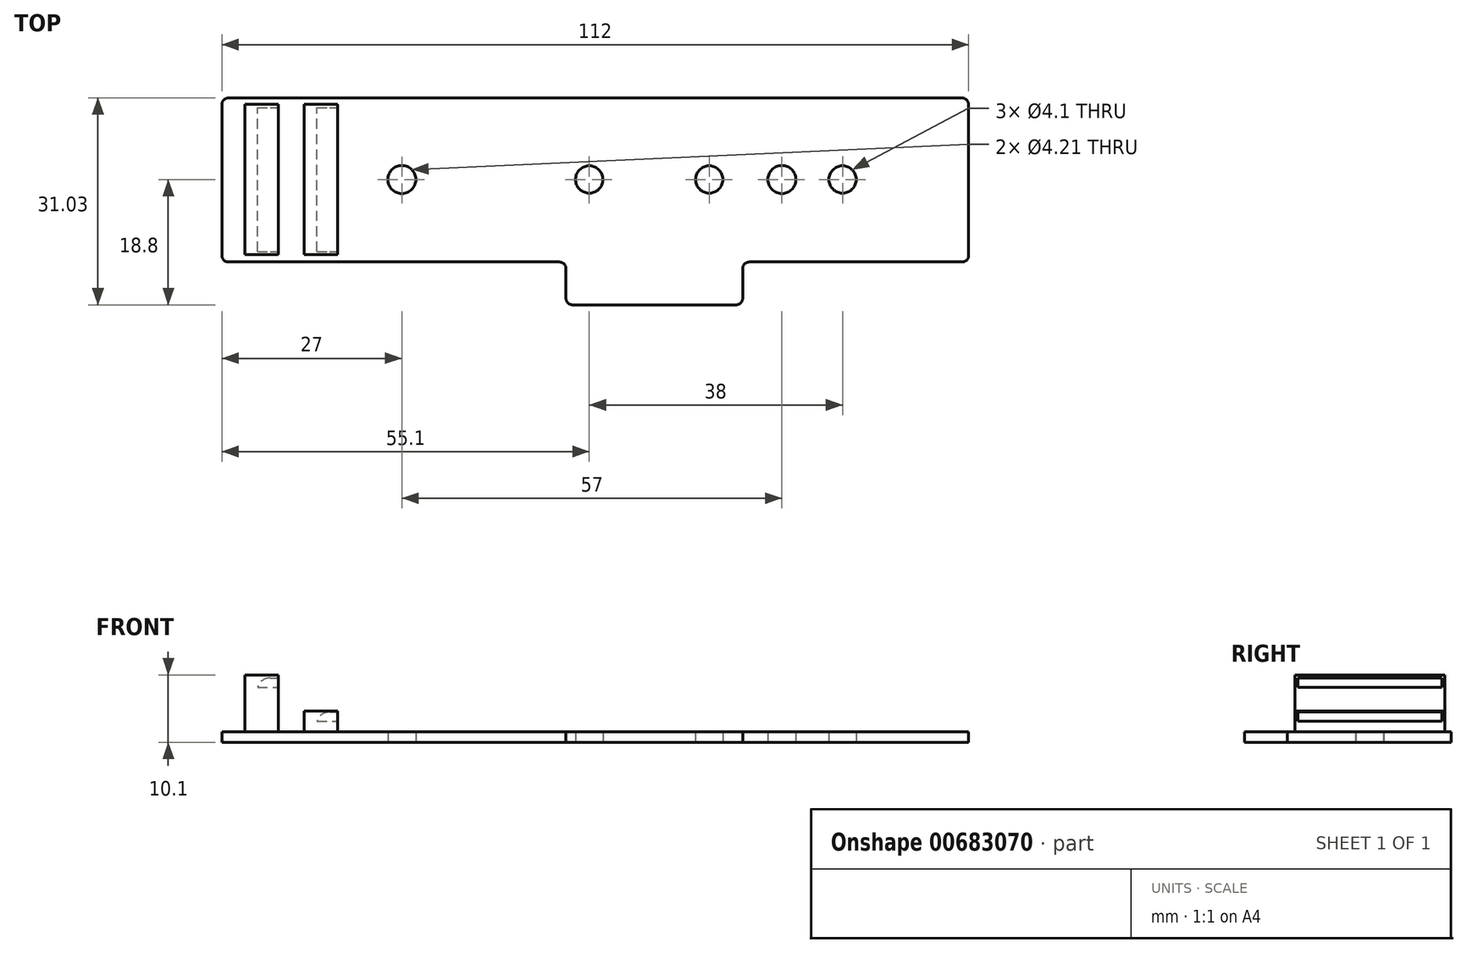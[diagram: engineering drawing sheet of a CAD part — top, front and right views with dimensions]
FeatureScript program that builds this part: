
annotation { "Feature Type Name" : "Feature", "Feature Type Description" : "" }
export const myFeature = defineFeature(function(context is Context, id is Id, definition is map)
    precondition{}
    {
        {
            assignVariable(context, id + "F0", {"name" : "M2conndepth", "anyValue" : 2.5});
        }
        {
            assignVariable(context, id + "F1", {"name" : "M2ssockheight", "anyValue" : 3.1});
        }
        {
            assignVariable(context, id + "F2", {"name" : "M2tsocketheight", "anyValue" : 8.5});
        }
        {
            assignVariable(context, id + "F3", {"name" : "PCBthick", "anyValue" : 1.6});
        }
        {
            var Q0;
            Q0=qCreatedBy(makeId("Top.planeOp"),FACE);
            var sketch = newSketch(context, id + "F4", { "sketchPlane" : qUnion([Q0])});
            skCircle(sketch, "E0", {"center": v(0, 0) * mm, "radius": 2.1 * mm});
            skLineSegment(sketch, "E1", {"start": v(0, 0) * mm, "end": v(-27, 0) * mm, "construction": true});
            skLineSegment(sketch, "E2", {"start": v(0, 0) * mm, "end": v(85, 0) * mm, "construction": true});
            skLineSegment(sketch, "E3.bottom", {"start": v(-27, 12.23) * mm, "end": v(85, 12.23) * mm});
            skLineSegment(sketch, "E3.top", {"start": v(-27, -12.37) * mm, "end": v(85, -12.37) * mm});
            skLineSegment(sketch, "E3.left", {"start": v(-27, 12.23) * mm, "end": v(-27, -12.37) * mm});
            skLineSegment(sketch, "E3.right", {"start": v(85, 12.23) * mm, "end": v(85, -12.37) * mm});
            skLineSegment(sketch, "E4", {"start": v(0, 0) * mm, "end": v(0, -12.37) * mm, "construction": true});
            skLineSegment(sketch, "E5", {"start": v(0, 0) * mm, "end": v(0, 12.23) * mm, "construction": true});
            skLineSegment(sketch, "E6", {"start": v(-17.03, -12.37) * mm, "end": v(0, -12.37) * mm, "construction": true});
            skLineSegment(sketch, "E7.bottom", {"start": v(-17.03, -12.37) * mm, "end": v(22.42, -12.37) * mm});
            skLineSegment(sketch, "E7.top", {"start": v(-17.03, -18.8) * mm, "end": v(22.42, -18.8) * mm});
            skLineSegment(sketch, "E7.left", {"start": v(-17.03, -12.37) * mm, "end": v(-17.03, -18.8) * mm});
            skLineSegment(sketch, "E7.right", {"start": v(22.42, -12.37) * mm, "end": v(22.42, -18.8) * mm});
            skLineSegment(sketch, "E8", {"start": v(2.7, -18.8) * mm, "end": v(2.7, 0) * mm, "construction": true});
            skLineSegment(sketch, "E9", {"start": v(22.42, -18.8) * mm, "end": v(0, -18.8) * mm, "construction": true});
            skLineSegment(sketch, "E10", {"start": v(0, -22.98) * mm, "end": v(24.62, -22.98) * mm, "construction": true});
            skLineSegment(sketch, "E11.bottom", {"start": v(24.62, -18.8) * mm, "end": v(51.12, -18.8) * mm});
            skLineSegment(sketch, "E11.top", {"start": v(24.62, -12.37) * mm, "end": v(51.12, -12.37) * mm});
            skLineSegment(sketch, "E11.left", {"start": v(24.62, -18.8) * mm, "end": v(24.62, -12.37) * mm});
            skLineSegment(sketch, "E11.right", {"start": v(51.12, -18.8) * mm, "end": v(51.12, -12.37) * mm});
            skLineSegment(sketch, "E12", {"start": v(0, -27.13) * mm, "end": v(51.12, -27.13) * mm, "construction": true});
            skLineSegment(sketch, "E13", {"start": v(0, 29.48) * mm, "end": v(57, 29.48) * mm, "construction": true});
            skCircle(sketch, "E14", {"center": v(57, 0) * mm, "radius": 2.1 * mm});
            skLineSegment(sketch, "E15", {"start": v(0, 0) * mm, "end": v(28.1, 0) * mm, "construction": true});
            skCircle(sketch, "E16", {"center": v(28.1, 0) * mm, "radius": 2.05 * mm});
            skLineSegment(sketch, "E17", {"start": v(0, 3.77) * mm, "end": v(46.1, 3.77) * mm, "construction": true});
            skCircle(sketch, "E18", {"center": v(46.1, 0) * mm, "radius": 2.05 * mm});
            skLineSegment(sketch, "E19", {"start": v(0, 8.26) * mm, "end": v(66.1, 8.26) * mm, "construction": true});
            skCircle(sketch, "E20", {"center": v(66.1, 0) * mm, "radius": 2.05 * mm});
            skLineSegment(sketch, "E21", {"start": v(0, -12.37) * mm, "end": v(-17.03, -12.37) * mm, "construction": true});
            skSolve(sketch);
        }
        {
            var Q0;
            Q0=makeQuery(id+"F4.imprint","IMPRINT",FACE,{"disambiguationData":[TD([[makeQuery(id+"F4.imprint","IMPRINT",EDGE,{"derivedFrom":sQuery(id+"F4.wireOp",EDGE,"E7.bottom")}),-1.0]])]});
            var Q1;
            Q1=makeQuery(id+"F4.imprint","IMPRINT",FACE,{"disambiguationData":[TD([[makeQuery(id+"F4.imprint","IMPRINT",EDGE,{"derivedFrom":sQuery(id+"F4.wireOp",EDGE,"E11.bottom")}),1.0]])]});
            var Q2;
            Q2=makeQuery(id+"F4.imprint","IMPRINT",FACE,{"disambiguationData":[TD([[makeQuery(id+"F4.imprint","IMPRINT",EDGE,{"derivedFrom":sQuery(id+"F4.wireOp",EDGE,"E1Ta9aYJ-BLLR-yCvW-Tl3E-SsffV6xoofWQ.bottom")}),1.0]])]});
            var Q3;
            Q3=makeQuery(id+"F4.imprint","IMPRINT",FACE,{"disambiguationData":[TD([[makeQuery(id+"F4.imprint","IMPRINT",EDGE,{"derivedFrom":sQuery(id+"F4.wireOp",EDGE,"a8g1MiHS-Xpk4-FMXC-Xz5o-XKk2ycmWGk7U.bottom")}),1.0]])]});
            var Q4;
            Q4=makeQuery(id+"F4.imprint","IMPRINT",FACE,{"disambiguationData":[TD([[makeQuery(id+"F4.imprint","IMPRINT",EDGE,{"derivedFrom":sQuery(id+"F4.wireOp",EDGE,"YHdcBCCz-BpKQ-KRm3-anxo-6fSsjPzmbMLq.bottom")}),-1.0]])]});
            var Q5;
            Q5=makeQuery(id+"F4.imprint","IMPRINT",FACE,{"disambiguationData":[TD([[makeQuery(id+"F4.imprint","IMPRINT",EDGE,{"derivedFrom":sQuery(id+"F4.wireOp",EDGE,"E0")}),-1.0]])]});
            extrude(context, id + "F5", {"entities" : qUnion([Q0, Q1, Q2, Q3, Q4, Q5]), "depth" : (getVariable(context, 'PCBthick')) * mm});
        }
        {
            var Q0;
            Q0=makeQuery(id+"F5.opExtrude","CAP_FACE",FACE,{"disambiguationData":[OSD([sQuery(id+"F4.wireOp",EDGE,"E0"),sQuery(id+"F4.wireOp",EDGE,"E3.bottom"),sQuery(id+"F4.wireOp",EDGE,"E3.top"),sQuery(id+"F4.wireOp",EDGE,"E3.left"),sQuery(id+"F4.wireOp",EDGE,"E3.right"),sQuery(id+"F4.wireOp",EDGE,"E7.top"),sQuery(id+"F4.wireOp",EDGE,"E7.left"),sQuery(id+"F4.wireOp",EDGE,"E7.right"),sQuery(id+"F4.wireOp",EDGE,"E11.bottom"),sQuery(id+"F4.wireOp",EDGE,"E11.left"),sQuery(id+"F4.wireOp",EDGE,"E11.right"),sQuery(id+"F4.wireOp",EDGE,"E1Ta9aYJ-BLLR-yCvW-Tl3E-SsffV6xoofWQ.bottom"),sQuery(id+"F4.wireOp",EDGE,"E1Ta9aYJ-BLLR-yCvW-Tl3E-SsffV6xoofWQ.left"),sQuery(id+"F4.wireOp",EDGE,"E1Ta9aYJ-BLLR-yCvW-Tl3E-SsffV6xoofWQ.right"),sQuery(id+"F4.wireOp",EDGE,"a8g1MiHS-Xpk4-FMXC-Xz5o-XKk2ycmWGk7U.bottom"),sQuery(id+"F4.wireOp",EDGE,"a8g1MiHS-Xpk4-FMXC-Xz5o-XKk2ycmWGk7U.left"),sQuery(id+"F4.wireOp",EDGE,"a8g1MiHS-Xpk4-FMXC-Xz5o-XKk2ycmWGk7U.right"),sQuery(id+"F4.wireOp",EDGE,"YHdcBCCz-BpKQ-KRm3-anxo-6fSsjPzmbMLq.top"),sQuery(id+"F4.wireOp",EDGE,"YHdcBCCz-BpKQ-KRm3-anxo-6fSsjPzmbMLq.left"),sQuery(id+"F4.wireOp",EDGE,"YHdcBCCz-BpKQ-KRm3-anxo-6fSsjPzmbMLq.right"),sQuery(id+"F4.wireOp",EDGE,"E14"),sQuery(id+"F4.wireOp",EDGE,"fpiimDXm-HCbj-4bNC-FueZ-Qats7nAzrHHA"),sQuery(id+"F4.wireOp",EDGE,"E16"),sQuery(id+"F4.wireOp",EDGE,"E18"),sQuery(id+"F4.wireOp",EDGE,"E20"),sQuery(id+"F4.wireOp",EDGE,"mZ1ixk2W-VYTq-aw9L-fxjL-cpEzxSfOFke0.top"),sQuery(id+"F4.wireOp",EDGE,"mZ1ixk2W-VYTq-aw9L-fxjL-cpEzxSfOFke0.left"),sQuery(id+"F4.wireOp",EDGE,"mZ1ixk2W-VYTq-aw9L-fxjL-cpEzxSfOFke0.right")])],"isStart":false});
            var sketch = newSketch(context, id + "F6", { "sketchPlane" : qUnion([Q0])});
            skLineSegment(sketch, "E22.bottom", {"start": v(-14.65, 11.25) * mm, "end": v(-9.65, 11.25) * mm});
            skLineSegment(sketch, "E22.top", {"start": v(-14.65, -11.25) * mm, "end": v(-9.65, -11.25) * mm});
            skLineSegment(sketch, "E22.left", {"start": v(-14.65, 11.25) * mm, "end": v(-14.65, -11.25) * mm});
            skLineSegment(sketch, "E22.right", {"start": v(-9.65, 11.25) * mm, "end": v(-9.65, -11.25) * mm});
            skLineSegment(sketch, "E23.bottom", {"start": v(-23.55, -11.25) * mm, "end": v(-18.55, -11.25) * mm});
            skLineSegment(sketch, "E23.top", {"start": v(-23.55, 11.25) * mm, "end": v(-18.55, 11.25) * mm});
            skLineSegment(sketch, "E23.left", {"start": v(-23.55, -11.25) * mm, "end": v(-23.55, 11.25) * mm});
            skLineSegment(sketch, "E23.right", {"start": v(-18.55, -11.25) * mm, "end": v(-18.55, 11.25) * mm});
            skPoint(sketch, "E23.middle", {"position": v(-21.05, 0) * mm});
            skCircle(sketch, "E24.0", {"center": v(0, 0) * mm, "radius": 2.1 * mm, "construction": true});
            skLineSegment(sketch, "E25", {"start": v(0, 0) * mm, "end": v(-21.05, 0) * mm, "construction": true});
            skLineSegment(sketch, "E26", {"start": v(0, 0) * mm, "end": v(-12.15, 0) * mm});
            skLineSegment(sketch, "E27", {"start": v(-14.65, 11.25) * mm, "end": v(-9.65, -11.25) * mm, "construction": true});
            skPoint(sketch, "E28", {"position": v(-12.15, 0) * mm});
            skSolve(sketch);
        }
        {
            var Q0;
            Q0=makeQuery(id+"F6.imprint","IMPRINT",FACE,{"disambiguationData":[TD([[makeQuery(id+"F6.imprint","IMPRINT",EDGE,{"derivedFrom":sQuery(id+"F6.wireOp",EDGE,"E22.bottom")}),-1.0]])]});
            extrude(context, id + "F7", {"entities" : qUnion([Q0]), "operationType" : NewBodyOperationType.ADD, "depth" : (getVariable(context, 'M2ssockheight')) * mm, "offsetDistance" : 25 * mm});
        }
        {
            var Q0;
            Q0=makeQuery(id+"F6.imprint","IMPRINT",FACE,{"disambiguationData":[TD([[makeQuery(id+"F6.imprint","IMPRINT",EDGE,{"derivedFrom":sQuery(id+"F6.wireOp",EDGE,"E23.bottom")}),1.0]])]});
            extrude(context, id + "F8", {"entities" : qUnion([Q0]), "operationType" : NewBodyOperationType.ADD, "depth" : (getVariable(context, 'M2tsocketheight')) * mm, "offsetDistance" : 25 * mm});
        }
        {
            var Q0;
            Q0=makeQuery(id+"F5.opExtrude","SWEPT_EDGE",EDGE,{"disambiguationData":[OSD([sQuery(id+"F4.wireOp",EDGE,"E3.top"),sQuery(id+"F4.wireOp",EDGE,"E3.left")])]});
            var Q1;
            Q1=makeQuery(id+"F5.opExtrude","SWEPT_EDGE",EDGE,{"disambiguationData":[OSD([sQuery(id+"F4.wireOp",EDGE,"E3.top"),sQuery(id+"F4.wireOp",EDGE,"E7.bottom"),sQuery(id+"F4.wireOp",EDGE,"E7.left")])]});
            var Q2;
            Q2=makeQuery(id+"F5.opExtrude","SWEPT_EDGE",EDGE,{"disambiguationData":[OSD([sQuery(id+"F4.wireOp",EDGE,"E7.top"),sQuery(id+"F4.wireOp",EDGE,"E7.left")])]});
            var Q3;
            Q3=makeQuery(id+"F5.opExtrude","SWEPT_EDGE",EDGE,{"disambiguationData":[OSD([sQuery(id+"F4.wireOp",EDGE,"E3.top"),sQuery(id+"F4.wireOp",EDGE,"E11.top"),sQuery(id+"F4.wireOp",EDGE,"E11.left")])]});
            var Q4;
            Q4=makeQuery(id+"F5.opExtrude","SWEPT_EDGE",EDGE,{"disambiguationData":[OSD([sQuery(id+"F4.wireOp",EDGE,"E11.bottom"),sQuery(id+"F4.wireOp",EDGE,"E11.left")])]});
            var Q5;
            Q5=makeQuery(id+"F5.opExtrude","SWEPT_EDGE",EDGE,{"disambiguationData":[OSD([sQuery(id+"F4.wireOp",EDGE,"E7.top"),sQuery(id+"F4.wireOp",EDGE,"E7.right")])]});
            var Q6;
            Q6=makeQuery(id+"F5.opExtrude","SWEPT_EDGE",EDGE,{"disambiguationData":[OSD([sQuery(id+"F4.wireOp",EDGE,"E11.bottom"),sQuery(id+"F4.wireOp",EDGE,"E11.right")])]});
            var Q7;
            Q7=makeQuery(id+"F5.opExtrude","SWEPT_EDGE",EDGE,{"disambiguationData":[OSD([sQuery(id+"F4.wireOp",EDGE,"E3.top"),sQuery(id+"F4.wireOp",EDGE,"E1Ta9aYJ-BLLR-yCvW-Tl3E-SsffV6xoofWQ.top"),sQuery(id+"F4.wireOp",EDGE,"E1Ta9aYJ-BLLR-yCvW-Tl3E-SsffV6xoofWQ.left")])]});
            var Q8;
            Q8=makeQuery(id+"F5.opExtrude","SWEPT_EDGE",EDGE,{"disambiguationData":[OSD([sQuery(id+"F4.wireOp",EDGE,"E1Ta9aYJ-BLLR-yCvW-Tl3E-SsffV6xoofWQ.bottom"),sQuery(id+"F4.wireOp",EDGE,"E1Ta9aYJ-BLLR-yCvW-Tl3E-SsffV6xoofWQ.left")])]});
            var Q9;
            Q9=makeQuery(id+"F5.opExtrude","SWEPT_EDGE",EDGE,{"disambiguationData":[OSD([sQuery(id+"F4.wireOp",EDGE,"E1Ta9aYJ-BLLR-yCvW-Tl3E-SsffV6xoofWQ.bottom"),sQuery(id+"F4.wireOp",EDGE,"E1Ta9aYJ-BLLR-yCvW-Tl3E-SsffV6xoofWQ.right")])]});
            var Q10;
            Q10=makeQuery(id+"F5.opExtrude","SWEPT_EDGE",EDGE,{"disambiguationData":[OSD([sQuery(id+"F4.wireOp",EDGE,"a8g1MiHS-Xpk4-FMXC-Xz5o-XKk2ycmWGk7U.bottom"),sQuery(id+"F4.wireOp",EDGE,"a8g1MiHS-Xpk4-FMXC-Xz5o-XKk2ycmWGk7U.left")])]});
            var Q11;
            Q11=makeQuery(id+"F5.opExtrude","SWEPT_EDGE",EDGE,{"disambiguationData":[OSD([sQuery(id+"F4.wireOp",EDGE,"a8g1MiHS-Xpk4-FMXC-Xz5o-XKk2ycmWGk7U.bottom"),sQuery(id+"F4.wireOp",EDGE,"a8g1MiHS-Xpk4-FMXC-Xz5o-XKk2ycmWGk7U.right")])]});
            var Q12;
            Q12=makeQuery(id+"F5.opExtrude","SWEPT_EDGE",EDGE,{"disambiguationData":[OSD([sQuery(id+"F4.wireOp",EDGE,"E3.top"),sQuery(id+"F4.wireOp",EDGE,"YHdcBCCz-BpKQ-KRm3-anxo-6fSsjPzmbMLq.bottom"),sQuery(id+"F4.wireOp",EDGE,"YHdcBCCz-BpKQ-KRm3-anxo-6fSsjPzmbMLq.left")])]});
            var Q13;
            Q13=makeQuery(id+"F5.opExtrude","SWEPT_EDGE",EDGE,{"disambiguationData":[OSD([sQuery(id+"F4.wireOp",EDGE,"YHdcBCCz-BpKQ-KRm3-anxo-6fSsjPzmbMLq.top"),sQuery(id+"F4.wireOp",EDGE,"YHdcBCCz-BpKQ-KRm3-anxo-6fSsjPzmbMLq.left")])]});
            var Q14;
            Q14=makeQuery(id+"F5.opExtrude","SWEPT_EDGE",EDGE,{"disambiguationData":[OSD([sQuery(id+"F4.wireOp",EDGE,"E3.top"),sQuery(id+"F4.wireOp",EDGE,"E7.bottom"),sQuery(id+"F4.wireOp",EDGE,"E7.right")])]});
            var Q15;
            Q15=makeQuery(id+"F5.opExtrude","SWEPT_EDGE",EDGE,{"disambiguationData":[OSD([sQuery(id+"F4.wireOp",EDGE,"E3.top"),sQuery(id+"F4.wireOp",EDGE,"E11.top"),sQuery(id+"F4.wireOp",EDGE,"E11.right")])]});
            var Q16;
            Q16=makeQuery(id+"F5.opExtrude","SWEPT_EDGE",EDGE,{"disambiguationData":[OSD([sQuery(id+"F4.wireOp",EDGE,"mZ1ixk2W-VYTq-aw9L-fxjL-cpEzxSfOFke0.top"),sQuery(id+"F4.wireOp",EDGE,"mZ1ixk2W-VYTq-aw9L-fxjL-cpEzxSfOFke0.left")])]});
            var Q17;
            Q17=makeQuery(id+"F5.opExtrude","SWEPT_EDGE",EDGE,{"disambiguationData":[OSD([sQuery(id+"F4.wireOp",EDGE,"E3.top"),sQuery(id+"F4.wireOp",EDGE,"a8g1MiHS-Xpk4-FMXC-Xz5o-XKk2ycmWGk7U.top"),sQuery(id+"F4.wireOp",EDGE,"a8g1MiHS-Xpk4-FMXC-Xz5o-XKk2ycmWGk7U.right")])]});
            var Q18;
            Q18=makeQuery(id+"F5.opExtrude","SWEPT_EDGE",EDGE,{"disambiguationData":[OSD([sQuery(id+"F4.wireOp",EDGE,"YHdcBCCz-BpKQ-KRm3-anxo-6fSsjPzmbMLq.top"),sQuery(id+"F4.wireOp",EDGE,"YHdcBCCz-BpKQ-KRm3-anxo-6fSsjPzmbMLq.right")])]});
            var Q19;
            Q19=makeQuery(id+"F5.opExtrude","SWEPT_EDGE",EDGE,{"disambiguationData":[OSD([sQuery(id+"F4.wireOp",EDGE,"E3.bottom"),sQuery(id+"F4.wireOp",EDGE,"E3.right")])]});
            var Q20;
            Q20=makeQuery(id+"F5.opExtrude","SWEPT_EDGE",EDGE,{"disambiguationData":[OSD([sQuery(id+"F4.wireOp",EDGE,"E3.bottom"),sQuery(id+"F4.wireOp",EDGE,"E3.left")])]});
            var Q21;
            Q21=makeQuery(id+"F5.opExtrude","SWEPT_EDGE",EDGE,{"disambiguationData":[OSD([sQuery(id+"F4.wireOp",EDGE,"mZ1ixk2W-VYTq-aw9L-fxjL-cpEzxSfOFke0.top"),sQuery(id+"F4.wireOp",EDGE,"mZ1ixk2W-VYTq-aw9L-fxjL-cpEzxSfOFke0.right")])]});
            fillet(context, id + "F9", {"entities" : qUnion([Q0, Q1, Q2, Q3, Q4, Q5, Q6, Q7, Q8, Q9, Q10, Q11, Q12, Q13, Q14, Q15, Q16, Q17, Q18, Q19, Q20, Q21]), "radius" : 1 * mm, "tangentPropagation" : true, "allowEdgeOverflow" : false});
        }
        {
            var Q0;
            Q0=makeQuery(id+"F7.opExtrude","SWEPT_FACE",FACE,{"disambiguationData":[OSD([sQuery(id+"F6.wireOp",EDGE,"E22.right")])]});
            var sketch = newSketch(context, id + "F10", { "sketchPlane" : qUnion([Q0])});
            skLineSegment(sketch, "E29", {"start": v(0, 1.6) * mm, "end": v(0, 3.14) * mm, "construction": true});
            skLineSegment(sketch, "E30.bottom", {"start": v(-10.8, 3.14) * mm, "end": v(10.8, 3.14) * mm});
            skLineSegment(sketch, "E30.top", {"start": v(-10.8, 4.54) * mm, "end": v(10.8, 4.54) * mm});
            skLineSegment(sketch, "E30.left", {"start": v(-10.8, 3.14) * mm, "end": v(-10.8, 4.54) * mm});
            skLineSegment(sketch, "E30.right", {"start": v(10.8, 3.14) * mm, "end": v(10.8, 4.54) * mm});
            skSolve(sketch);
        }
        {
            var Q0;
            Q0=makeQuery(id+"F10.imprint","IMPRINT",FACE,{"disambiguationData":[TD([[makeQuery(id+"F10.imprint","IMPRINT",EDGE,{"derivedFrom":sQuery(id+"F10.wireOp",EDGE,"E30.bottom")}),1.0]])]});
            extrude(context, id + "F11", {"entities" : qUnion([Q0]), "operationType" : NewBodyOperationType.REMOVE, "oppositeDirection" : true, "depth" : (getVariable(context, 'M2conndepth') + .6) * mm, "offsetDistance" : 25 * mm});
        }
        {
            var Q0;
            Q0=makeQuery(id+"F11.boolean.opBoolean","COPY",EDGE,{"derivedFrom":makeQuery(id+"F11.opExtrude","CAP_EDGE",EDGE,{"disambiguationData":[OSD([sQuery(id+"F10.wireOp",EDGE,"E30.top")])],"isStart":false})});
            fillet(context, id + "F12", {"entities" : qUnion([Q0]), "radius" : 2 * mm, "tangentPropagation" : true, "allowEdgeOverflow" : false});
        }
        {
            var Q0;
            Q0=makeQuery(id+"F8.opExtrude","SWEPT_FACE",FACE,{"disambiguationData":[OSD([sQuery(id+"F6.wireOp",EDGE,"E23.right")])]});
            var sketch = newSketch(context, id + "F13", { "sketchPlane" : qUnion([Q0])});
            skLineSegment(sketch, "E31", {"start": v(0, 1.6) * mm, "end": v(0, 8.25) * mm, "construction": true});
            skLineSegment(sketch, "E32.bottom", {"start": v(-10.8, 8.25) * mm, "end": v(10.8, 8.25) * mm});
            skLineSegment(sketch, "E32.top", {"start": v(-10.8, 9.65) * mm, "end": v(10.8, 9.65) * mm});
            skLineSegment(sketch, "E32.left", {"start": v(-10.8, 8.25) * mm, "end": v(-10.8, 9.65) * mm});
            skLineSegment(sketch, "E32.right", {"start": v(10.8, 8.25) * mm, "end": v(10.8, 9.65) * mm});
            skSolve(sketch);
        }
        {
            var Q0;
            Q0=makeQuery(id+"F13.imprint","IMPRINT",FACE,{"disambiguationData":[TD([[makeQuery(id+"F13.imprint","IMPRINT",EDGE,{"derivedFrom":sQuery(id+"F13.wireOp",EDGE,"E32.bottom")}),1.0]])]});
            extrude(context, id + "F14", {"entities" : qUnion([Q0]), "operationType" : NewBodyOperationType.REMOVE, "oppositeDirection" : true, "depth" : (getVariable(context, 'M2conndepth') + .6) * mm, "offsetDistance" : 25 * mm});
        }
        {
            var Q0;
            Q0=makeQuery(id+"F14.boolean.opBoolean","COPY",EDGE,{"derivedFrom":makeQuery(id+"F14.opExtrude","CAP_EDGE",EDGE,{"disambiguationData":[OSD([sQuery(id+"F13.wireOp",EDGE,"E32.top")])],"isStart":false})});
            fillet(context, id + "F15", {"entities" : qUnion([Q0]), "radius" : 2 * mm, "tangentPropagation" : true, "allowEdgeOverflow" : false});
        }
    });
